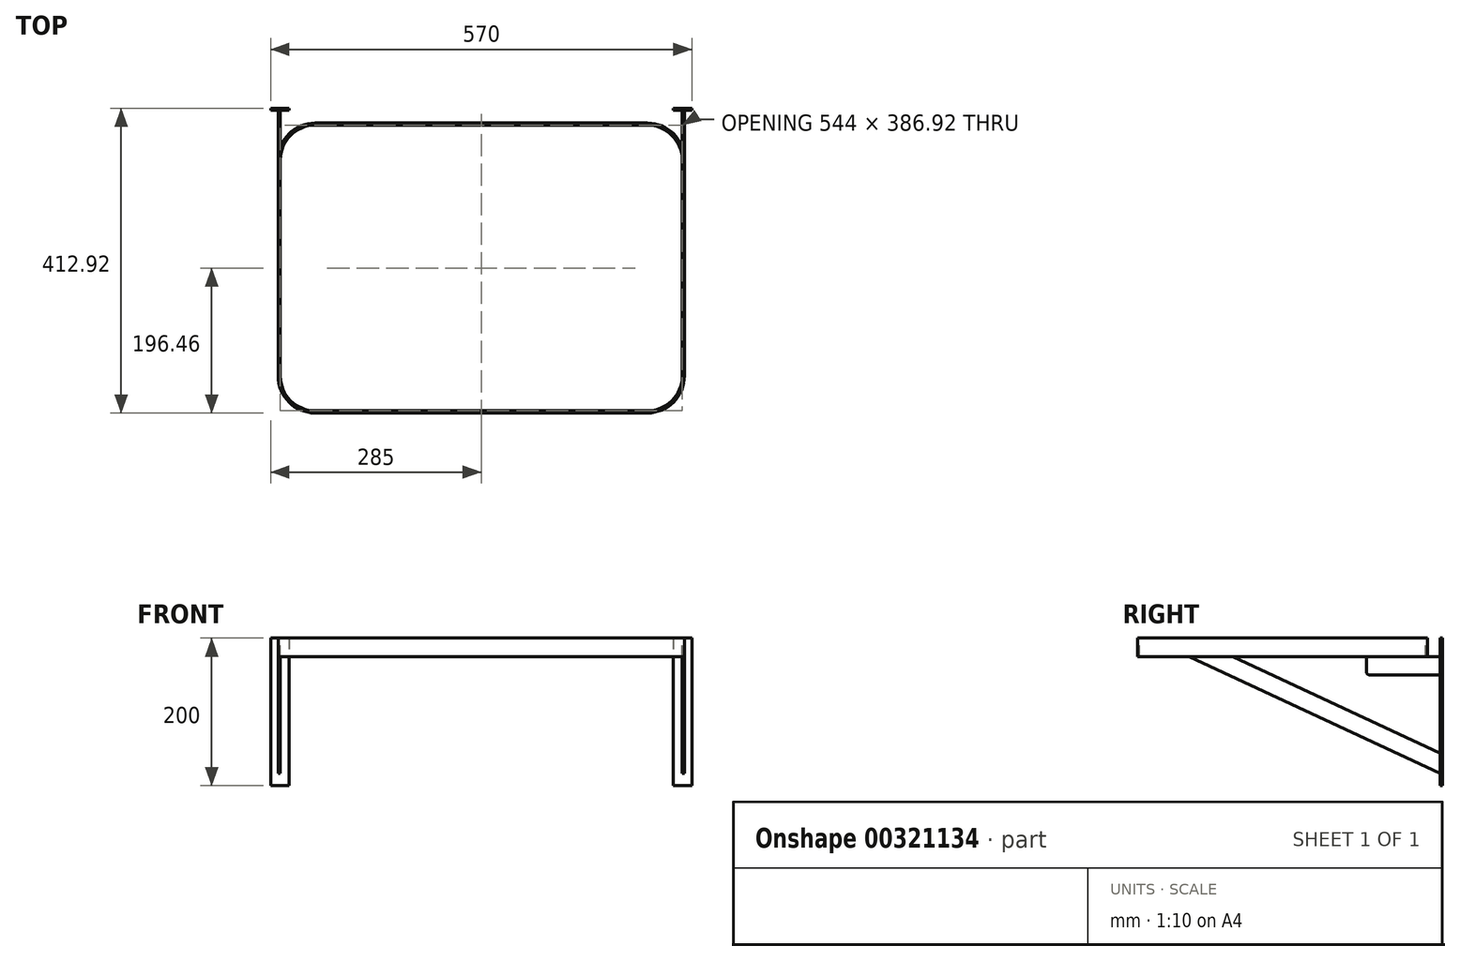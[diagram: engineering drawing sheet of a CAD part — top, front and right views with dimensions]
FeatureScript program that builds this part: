
annotation { "Feature Type Name" : "Feature", "Feature Type Description" : "" }
export const myFeature = defineFeature(function(context is Context, id is Id, definition is map)
    precondition{}
    {
        {
            var Q0;
            Q0=qCreatedBy(makeId("Top.planeOp"),FACE);
            var sketch = newSketch(context, id + "F0", { "sketchPlane" : qUnion([Q0])});
            skLineSegment(sketch, "E0", {"start": v(-225, -20) * mm, "end": v(225, -20) * mm});
            skLineSegment(sketch, "E1", {"start": v(-225, -412.92) * mm, "end": v(225, -412.92) * mm});
            skLineSegment(sketch, "E2", {"start": v(275, -70) * mm, "end": v(275, -362.92) * mm});
            skLineSegment(sketch, "E3", {"start": v(-275, -70) * mm, "end": v(-275, -362.92) * mm});
            skArc(sketch, "E4", {"start": v(-225, -20) * mm, "mid": v(-260.36, -34.64) * mm, "end": v(-275, -70) * mm});
            skArc(sketch, "E5", {"start": v(-275, -362.92) * mm, "mid": v(-260.36, -398.28) * mm, "end": v(-225, -412.92) * mm});
            skArc(sketch, "E6", {"start": v(225, -412.92) * mm, "mid": v(260.36, -398.28) * mm, "end": v(275, -362.92) * mm});
            skArc(sketch, "E7", {"start": v(275, -70) * mm, "mid": v(260.36, -34.64) * mm, "end": v(225, -20) * mm});
            skArc(sketch, "E8.0", {"start": v(-225, -23) * mm, "mid": v(-258.23, -36.77) * mm, "end": v(-272, -70) * mm});
            skLineSegment(sketch, "E8.1", {"start": v(-272, -70) * mm, "end": v(-272, -362.92) * mm});
            skLineSegment(sketch, "E8.2", {"start": v(-225, -23) * mm, "end": v(225, -23) * mm});
            skArc(sketch, "E8.3", {"start": v(-272, -362.92) * mm, "mid": v(-258.23, -396.15) * mm, "end": v(-225, -409.92) * mm});
            skArc(sketch, "E8.4", {"start": v(272, -70) * mm, "mid": v(258.23, -36.77) * mm, "end": v(225, -23) * mm});
            skLineSegment(sketch, "E8.5", {"start": v(272, -70) * mm, "end": v(272, -362.92) * mm});
            skArc(sketch, "E8.6", {"start": v(225, -409.92) * mm, "mid": v(258.23, -396.15) * mm, "end": v(272, -362.92) * mm});
            skLineSegment(sketch, "E8.7", {"start": v(-225, -409.92) * mm, "end": v(225, -409.92) * mm});
            skSolve(sketch);
        }
        {
            var Q0;
            Q0 = qSketchRegion(id + "F0", true);
            extrude(context, id + "F1", {"entities" : qUnion([Q0]), "oppositeDirection" : true, "depth" : 25 * mm});
        }
        {
            var Q0;
            Q0=qCreatedBy(makeId("Front.planeOp"),FACE);
            var sketch = newSketch(context, id + "F2", { "sketchPlane" : qUnion([Q0])});
            skLineSegment(sketch, "E9.bottom", {"start": v(-285, 0) * mm, "end": v(-260, 0) * mm});
            skLineSegment(sketch, "E9.top", {"start": v(-285, -200) * mm, "end": v(-260, -200) * mm});
            skLineSegment(sketch, "E9.left", {"start": v(-285, 0) * mm, "end": v(-285, -200) * mm});
            skLineSegment(sketch, "E9.right", {"start": v(-260, 0) * mm, "end": v(-260, -200) * mm});
            skLineSegment(sketch, "E10.bottom", {"start": v(260, 0) * mm, "end": v(285, 0) * mm});
            skLineSegment(sketch, "E10.top", {"start": v(260, -200) * mm, "end": v(285, -200) * mm});
            skLineSegment(sketch, "E10.left", {"start": v(260, 0) * mm, "end": v(260, -200) * mm});
            skLineSegment(sketch, "E10.right", {"start": v(285, 0) * mm, "end": v(285, -200) * mm});
            skSolve(sketch);
        }
        {
            var Q0;
            Q0 = qSketchRegion(id + "F2", true);
            extrude(context, id + "F3", {"entities" : qUnion([Q0]), "depth" : 3 * mm});
        }
        {
            var Q0;
            Q0=makeQuery(id+"F1.opExtrude","SWEPT_FACE",FACE,{"disambiguationData":[OSD([sQuery(id+"F0.wireOp",EDGE,"E3")])]});
            var sketch = newSketch(context, id + "F4", { "sketchPlane" : qUnion([Q0])});
            skLineSegment(sketch, "E11.bottom", {"start": v(3, -25) * mm, "end": v(103, -25) * mm});
            skLineSegment(sketch, "E11.top", {"start": v(3, -50) * mm, "end": v(103, -50) * mm});
            skLineSegment(sketch, "E11.left", {"start": v(3, -25) * mm, "end": v(3, -50) * mm});
            skLineSegment(sketch, "E11.right", {"start": v(103, -25) * mm, "end": v(103, -50) * mm});
            skLineSegment(sketch, "E12", {"start": v(3, -155.92) * mm, "end": v(283.77, -25) * mm});
            skLineSegment(sketch, "E13", {"start": v(283.77, -25) * mm, "end": v(342.92, -25) * mm});
            skLineSegment(sketch, "E14", {"start": v(342.92, -25) * mm, "end": v(3, -183.5) * mm});
            skLineSegment(sketch, "E15", {"start": v(3, -183.5) * mm, "end": v(3, -155.92) * mm});
            skSolve(sketch);
        }
        {
            var Q0;
            Q0 = qSketchRegion(id + "F4", true);
            extrude(context, id + "F5", {"entities" : qUnion([Q0]), "oppositeDirection" : true, "depth" : 3 * mm});
        }
        {
            var Q0;
            Q0=makeQuery(id+"F5.opExtrude","SWEPT_EDGE",EDGE,{"disambiguationData":[OSD([sQuery(id+"F4.wireOp",EDGE,"E11.top"),sQuery(id+"F4.wireOp",EDGE,"E11.right")])]});
            fillet(context, id + "F6", {"entities" : qUnion([Q0]), "radius" : 5 * mm, "tangentPropagation" : true, "allowEdgeOverflow" : false});
        }
        {
            var Q0;
            Q0=makeQuery(id+"F5.opExtrude","SWEPT_BODY",BODY,{"disambiguationData":[OSD([sQuery(id+"F4.wireOp",EDGE,"E11.bottom"),sQuery(id+"F4.wireOp",EDGE,"E11.top"),sQuery(id+"F4.wireOp",EDGE,"E11.left"),sQuery(id+"F4.wireOp",EDGE,"E11.right")])]});
            var Q1;
            Q1=makeQuery(id+"F5.opExtrude","SWEPT_BODY",BODY,{"disambiguationData":[OSD([sQuery(id+"F4.wireOp",EDGE,"E12"),sQuery(id+"F4.wireOp",EDGE,"E13"),sQuery(id+"F4.wireOp",EDGE,"E14"),sQuery(id+"F4.wireOp",EDGE,"E15")])]});
            var Q2;
            Q2=qCreatedBy(makeId("Right.planeOp"),FACE);
            mirror(context, id + "F7", {"entities" : qUnion([Q0, Q1]), "mirrorPlane" : qUnion([Q2])});
        }
    });
